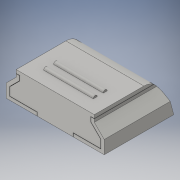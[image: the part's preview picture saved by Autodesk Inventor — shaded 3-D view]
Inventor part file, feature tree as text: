
AUTODESK INVENTOR PART (.ipt)
format: ipt  version: 2016 (Build 200138000, 138)  size: 324,608 bytes
history: native  units: mm
features: sketch x14, extrude x12, plane x1, sweep x1, mirror x1, projected_geometry x1
ambient origin geometry x8: Origin, YZ Plane, XZ Plane, XY Plane, X Axis, Y Axis, Z Axis, Center Point
bodies: Solid1 (feature_tree), Solid2 (feature_tree)
feature tree (30):
  extrude  "Extrusion1"  TaperAngle=45.0deg  [1 undecoded]
  sketch  "Sketch5"  dims[d4=3.0mm d5=3.0mm]
  extrude  "Extrusion3"  Depth=7.0mm
  extrude  "Extrusion2"  Depth=3.0mm
  extrude  "Extrusion4"  Depth=9.0mm
  extrude  "Extrusion5"  Depth=21.0mm TaperAngle=0.0deg
  extrude  "Extrusion7"  Depth=2.0mm
  extrude  "Extrusion13"  Depth=11.0mm
  extrude  "Extrusion15"  Depth=6.8mm TaperAngle=0.0deg
  extrude  "Extrusion16"  Depth=16.0mm
  extrude  "Extrusion17"  Depth=3.1mm
  plane  "Work Plane1"
  extrude  "Extrusion18"  Depth=1.0mm TaperAngle=0.0deg
  extrude  "Extrusion19"  Depth=20.3mm
  sweep  "Sweep1"
  mirror  "Mirror2"
  sketch  "Sketch2"  dims[d0=45.0deg d1=45.0deg]
  sketch  "Sketch4"  dims[d2=29.6mm d3=7.0mm]
  sketch  "Sketch6"  dims[d6=7.0mm d7=9.0mm]
  sketch  "Sketch7"  dims[d8=1.0mm d9=21.0mm d10=0.0mm]
  sketch  "Sketch10"  dims[d13=6.8mm d14=0.0mm d15=2.0mm]
  sketch  "Sketch18"  dims[d16=7.0mm d17=11.0mm]
  sketch  "Sketch25"  dims[d18=1.6mm d19=6.8mm d20=0.0mm]
  sketch  "Sketch27"  dims[d21=4.7mm d22=16.0mm]
  sketch  "Sketch28"  dims[d23=6.0mm d24=3.1mm]
  sketch  "Sketch29"  dims[d25=6.8mm d26=0.0mm d29=1.0mm d30=0.0mm]
  sketch  "Sketch30"  dims[d34=15.0mm d35=20.3mm]
  projected_geometry  "Projected Loop5"
  sketch  "Sketch34"  dims[d36=4.0mm d37=0.0mm d48=1.0mm d55=1.1mm d56=0.0mm d57=0.0mm d66=1.0mm d67=0.1mm d68=1.0mm d69=0.0mm d70=0.1mm d72=1.0mm d73=0.0mm d74=0.1mm d75=1.0mm d76=0.0mm d77=24.0mm d78=7.9mm d79=4.0mm d80=0.0mm d81=0.0mm d83=0.6mm d84=3.0mm d85=4.0mm d86=15.0mm d87=0.0mm d88=1.2mm d89=0.1mm d90=0.1mm d102=1.0mm d103=1.1mm d104=45.0deg d105=0.0mm d106=0.0mm]
  sketch  "3D Sketch1"
note: 1 required parameter value undecoded (feature->parameter linkage not recoverable at this tier; creation-order binding heuristic only, values carry confidence <= 0.55)
